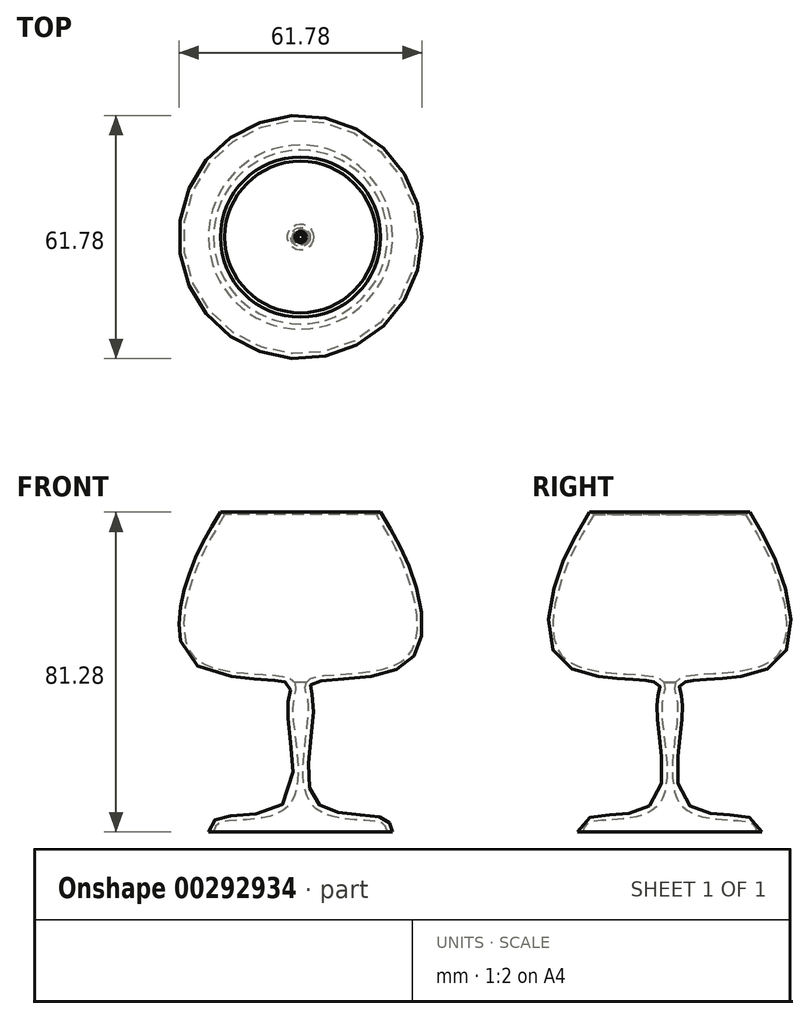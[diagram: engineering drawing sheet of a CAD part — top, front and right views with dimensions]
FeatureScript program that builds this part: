
annotation { "Feature Type Name" : "Feature", "Feature Type Description" : "" }
export const myFeature = defineFeature(function(context is Context, id is Id, definition is map)
    precondition{}
    {
        {
            var Q0;
            Q0=qCreatedBy(makeId("Front.planeOp"),FACE);
            var sketch = newSketch(context, id + "F0", { "sketchPlane" : qUnion([Q0])});
            skFitSpline(sketch, "E0", {"points": [v(23.39, 0) * mm, v(20.97, 3.54) * mm, v(3.93, 7.7) * mm, v(3.26, 32.8) * mm, v(2.99, 37.77) * mm, v(26.61, 42.47) * mm, v(28.92, 63.68) * mm, v(20.34, 81.28) * mm], "startDerivative": vector(-12.27, 56.59) * mm, "endDerivative": vector(-58.97, 97.42) * mm});
            skFitSpline(sketch, "E1.0", {"points": [v(22.15, -0.27) * mm, v(22.08, 0.03) * mm, v(21.96, 0.58) * mm, v(21.75, 1.24) * mm, v(21.47, 1.72) * mm, v(21.16, 2.02) * mm, v(20.77, 2.25) * mm, v(20.26, 2.47) * mm, v(19.27, 2.7) * mm, v(17.7, 2.88) * mm, v(15.86, 3) * mm, v(13.84, 3.13) * mm, v(11.73, 3.31) * mm, v(9.6, 3.6) * mm, v(7.52, 4.08) * mm, v(5.88, 4.7) * mm, v(4.67, 5.37) * mm, v(3.83, 5.98) * mm, v(3.07, 6.71) * mm, v(2.42, 7.56) * mm, v(1.9, 8.48) * mm, v(1.35, 9.8) * mm, v(0.9, 11.59) * mm, v(0.66, 13.9) * mm, v(0.65, 16.32) * mm, v(0.8, 18.83) * mm, v(1.04, 21.36) * mm, v(1.34, 23.86) * mm, v(1.64, 26.28) * mm, v(1.9, 28.54) * mm, v(2.05, 30.59) * mm, v(2.05, 32.05) * mm, v(1.96, 33.01) * mm, v(1.82, 33.9) * mm, v(1.62, 34.67) * mm, v(1.43, 35.38) * mm, v(1.3, 35.9) * mm, v(1.2, 36.45) * mm, v(1.17, 36.96) * mm, v(1.24, 37.41) * mm, v(1.35, 37.77) * mm, v(1.53, 38.1) * mm, v(1.85, 38.52) * mm, v(2.35, 38.9) * mm, v(2.99, 39.18) * mm, v(3.67, 39.38) * mm, v(4.42, 39.54) * mm, v(5.25, 39.67) * mm, v(6.45, 39.8) * mm, v(8.15, 39.94) * mm, v(10.4, 40.1) * mm, v(12.83, 40.26) * mm, v(15.33, 40.49) * mm, v(17.83, 40.8) * mm, v(20.24, 41.25) * mm, v(22.48, 41.84) * mm, v(24.12, 42.48) * mm, v(25.26, 43.09) * mm, v(26.01, 43.58) * mm, v(26.67, 44.13) * mm, v(27.45, 44.93) * mm, v(28.24, 46.06) * mm, v(28.93, 47.62) * mm, v(29.39, 49.38) * mm, v(29.7, 51.93) * mm, v(29.56, 55.43) * mm, v(28.88, 59.07) * mm, v(28.14, 61.9) * mm, v(27.3, 64.63) * mm, v(26.13, 67.8) * mm, v(24.56, 71.26) * mm, v(22.87, 74.5) * mm, v(21.1, 77.59) * mm, v(19.87, 79.61) * mm, v(19.25, 80.63) * mm]});
            skLineSegment(sketch, "E2", {"start": v(1.47, 37.98) * mm, "end": v(0, 37.98) * mm});
            skLineSegment(sketch, "E3", {"start": v(0, 37.98) * mm, "end": v(0, 0) * mm});
            skLineSegment(sketch, "E4", {"start": v(0, 0) * mm, "end": v(23.39, 0) * mm});
            skLineSegment(sketch, "E5", {"start": v(20.34, 81.28) * mm, "end": v(19.25, 80.63) * mm});
            skSolve(sketch);
        }
        {
            var Q0;
            Q0=makeQuery(id+"F0.imprint","IMPRINT",FACE,{"disambiguationData":[TD([[makeQuery(id+"F0.imprint","IMPRINT",EDGE,{"derivedFrom":sQuery(id+"F0.wireOp",EDGE,"E0")}),1.0]])]});
            var Q1;
            Q1=sQuery(id+"F0.wireOp",EDGE,"E3");
            revolve(context, id + "F1", {"entities" : qUnion([Q0]), "axis" : qUnion([Q1]), "revolveType" : RevolveType.FULL});
        }
    });
